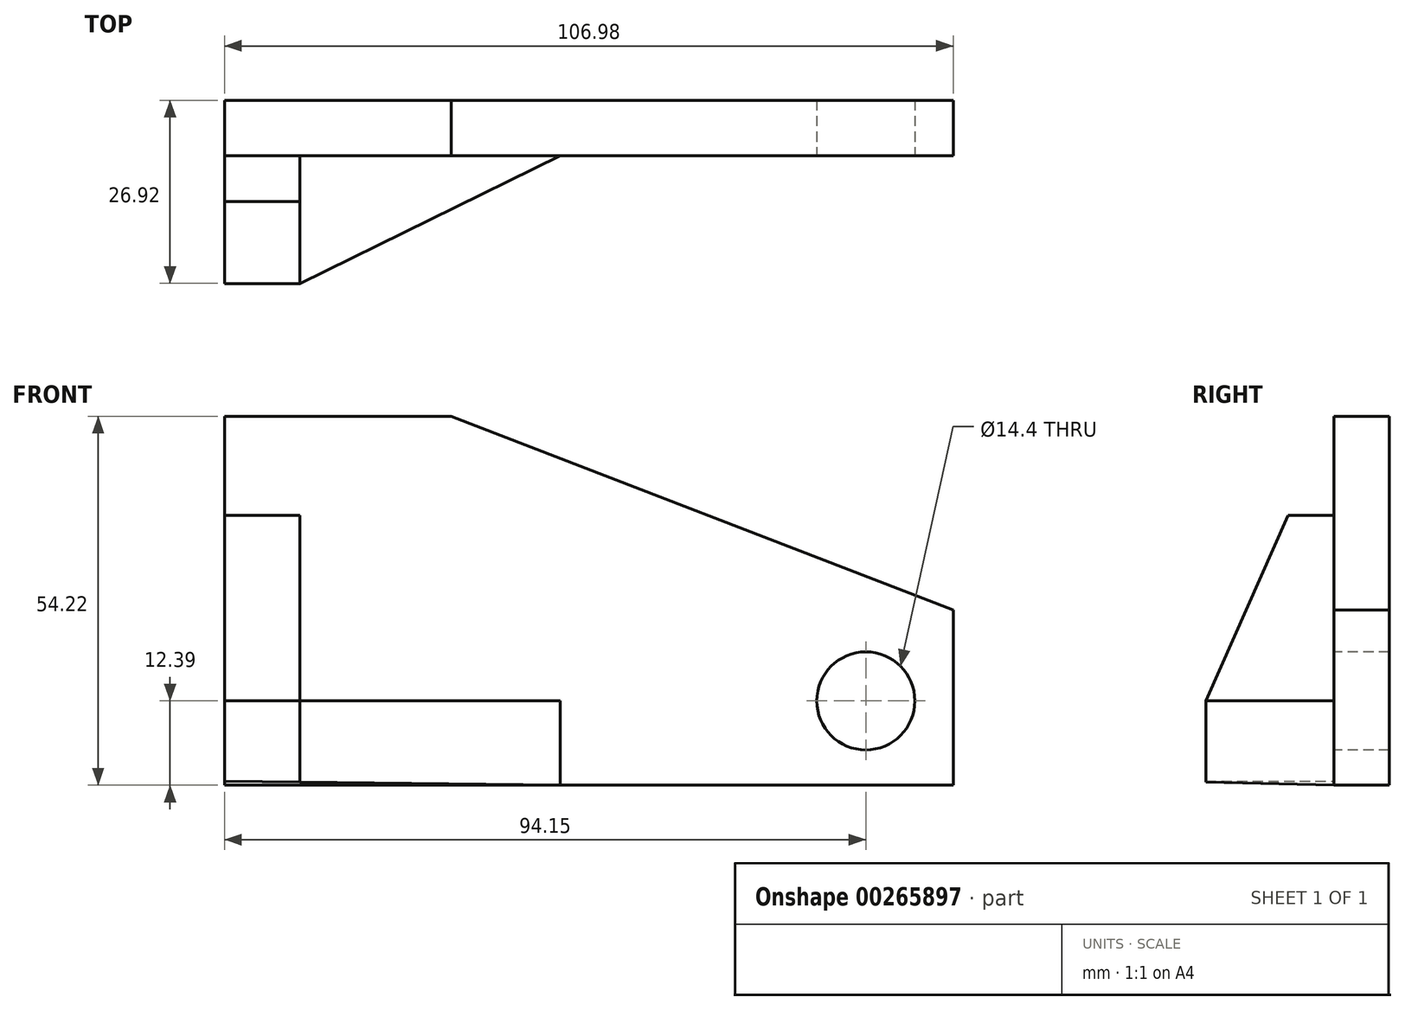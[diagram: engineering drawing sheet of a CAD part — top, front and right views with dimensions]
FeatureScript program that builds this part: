
annotation { "Feature Type Name" : "Feature", "Feature Type Description" : "" }
export const myFeature = defineFeature(function(context is Context, id is Id, definition is map)
    precondition{}
    {
        {
            var Q0;
            Q0=qCreatedBy(makeId("Front.planeOp"),FACE);
            var sketch = newSketch(context, id + "F0", { "sketchPlane" : qUnion([Q0])});
            skLineSegment(sketch, "E0", {"start": v(-56.55, 41.83) * mm, "end": v(-56.55, -12.39) * mm});
            skLineSegment(sketch, "E1", {"start": v(-56.55, -12.39) * mm, "end": v(50.43, -12.39) * mm});
            skLineSegment(sketch, "E2", {"start": v(50.43, -12.39) * mm, "end": v(50.43, 41.83) * mm});
            skLineSegment(sketch, "E3", {"start": v(50.43, 41.83) * mm, "end": v(-56.55, 41.83) * mm});
            skSolve(sketch);
        }
        {
            var Q0;
            Q0 = qSketchRegion(id + "F0", true);
            extrude(context, id + "F1", {"entities" : qUnion([Q0]), "depth" : 8.13 * mm});
        }
        {
            var Q0;
            Q0=makeQuery(id+"F1.opExtrude","CAP_FACE",FACE,{"disambiguationData":[OSD([sQuery(id+"F0.wireOp",EDGE,"E0"),sQuery(id+"F0.wireOp",EDGE,"E1"),sQuery(id+"F0.wireOp",EDGE,"E2"),sQuery(id+"F0.wireOp",EDGE,"E3")])],"isStart":false});
            var sketch = newSketch(context, id + "F2", { "sketchPlane" : qUnion([Q0])});
            skLineSegment(sketch, "E4", {"start": v(-33.81, 45.9) * mm, "end": v(61.2, 9.18) * mm});
            skSolve(sketch);
        }
        {
            var Q0;
            Q0 = qSketchRegion(id + "F2", true);
            var Q1;
            {var subQ0=sQuery(id+"F2.wireOp",EDGE,"E4");var subQ1=makeQuery(id+"F1.opExtrude","CAP_EDGE",EDGE,{"disambiguationData":[OSD([sQuery(id+"F0.wireOp",EDGE,"E2")])],"isStart":false});var subQ2=makeQuery(id+"F2.imprint","INTERSECT",VERTEX,{"derivedFrom":[subQ1,subQ0]});Q1=makeQuery(id+"F2.imprint","IMPRINT",FACE,{"disambiguationData":[TD([[makeQuery(id+"F2.imprint","IMPRINT",EDGE,{"disambiguationData":[TD([[subQ2,1.0]])],"derivedFrom":subQ0}),1.0]])]});}
            extrude(context, id + "F3", {"entities" : qUnion([Q0, Q1]), "operationType" : NewBodyOperationType.REMOVE, "oppositeDirection" : true, "depth" : 25.4 * mm});
        }
        {
            var Q0;
            Q0=makeQuery(id+"F1.opExtrude","CAP_FACE",FACE,{"disambiguationData":[OSD([sQuery(id+"F0.wireOp",EDGE,"E0"),sQuery(id+"F0.wireOp",EDGE,"E1"),sQuery(id+"F0.wireOp",EDGE,"E2"),sQuery(id+"F0.wireOp",EDGE,"E3")])],"isStart":false});
            var sketch = newSketch(context, id + "F4", { "sketchPlane" : qUnion([Q0])});
            skCircle(sketch, "E5", {"center": v(37.6, 0) * mm, "radius": 7.2 * mm});
            skSolve(sketch);
        }
        {
            var Q0;
            Q0 = qSketchRegion(id + "F4", true);
            extrude(context, id + "F5", {"entities" : qUnion([Q0]), "operationType" : NewBodyOperationType.REMOVE, "oppositeDirection" : true, "depth" : 25.4 * mm});
        }
        {
            var Q0;
            Q0=makeQuery(id+"F1.opExtrude","CAP_FACE",FACE,{"disambiguationData":[OSD([sQuery(id+"F0.wireOp",EDGE,"E0"),sQuery(id+"F0.wireOp",EDGE,"E1"),sQuery(id+"F0.wireOp",EDGE,"E2"),sQuery(id+"F0.wireOp",EDGE,"E3")])],"isStart":false});
            var sketch = newSketch(context, id + "F6", { "sketchPlane" : qUnion([Q0])});
            skLineSegment(sketch, "E6", {"start": v(-56.55, 27.25) * mm, "end": v(-56.55, -11.8) * mm});
            skLineSegment(sketch, "E7", {"start": v(-56.55, 27.25) * mm, "end": v(-45.47, 27.25) * mm});
            skLineSegment(sketch, "E8", {"start": v(-45.47, 27.25) * mm, "end": v(-45.47, 0) * mm});
            skLineSegment(sketch, "E9", {"start": v(-45.47, 0) * mm, "end": v(-7.29, 0) * mm});
            skLineSegment(sketch, "E10", {"start": v(-56.55, -11.8) * mm, "end": v(-7.29, -12.39) * mm});
            skLineSegment(sketch, "E11", {"start": v(-7.29, -12.39) * mm, "end": v(-7.29, 0) * mm});
            skSolve(sketch);
        }
        {
            var Q0;
            Q0 = qSketchRegion(id + "F6", true);
            extrude(context, id + "F7", {"entities" : qUnion([Q0]), "operationType" : NewBodyOperationType.ADD, "depth" : 18.8 * mm});
        }
        {
            var Q0;
            Q0=makeQuery(id+"F7.opExtrude","SWEPT_FACE",FACE,{"disambiguationData":[OSD([sQuery(id+"F6.wireOp",EDGE,"E9")])]});
            var sketch = newSketch(context, id + "F8", { "sketchPlane" : qUnion([Q0])});
            skLineSegment(sketch, "E12", {"start": v(-45.47, -26.92) * mm, "end": v(-7.29, -8.13) * mm});
            skSolve(sketch);
        }
        {
            var Q0;
            Q0=makeQuery(id+"F8.imprint","IMPRINT",FACE,{"disambiguationData":[TD([[makeQuery(id+"F8.imprint","IMPRINT",EDGE,{"derivedFrom":sQuery(id+"F8.wireOp",EDGE,"E12")}),-1.0]])]});
            extrude(context, id + "F9", {"entities" : qUnion([Q0]), "operationType" : NewBodyOperationType.REMOVE, "oppositeDirection" : true, "depth" : 25.4 * mm});
        }
        {
            var Q0;
            Q0=makeQuery(id+"F7.opExtrude","SWEPT_FACE",FACE,{"disambiguationData":[OSD([sQuery(id+"F6.wireOp",EDGE,"E8")])]});
            var sketch = newSketch(context, id + "F10", { "sketchPlane" : qUnion([Q0])});
            skLineSegment(sketch, "E13", {"start": v(-26.92, 0) * mm, "end": v(-14.87, 27.25) * mm});
            skSolve(sketch);
        }
        {
            var Q0;
            {var subQ0=sQuery(id+"F10.wireOp",EDGE,"E13");Q0=makeQuery(id+"F10.imprint","IMPRINT",FACE,{"disambiguationData":[TD([[makeQuery(id+"F10.imprint","IMPRINT",EDGE,{"derivedFrom":subQ0}),1.0]])]});}
            extrude(context, id + "F11", {"entities" : qUnion([Q0]), "operationType" : NewBodyOperationType.REMOVE, "oppositeDirection" : true, "depth" : 25.4 * mm});
        }
    });
